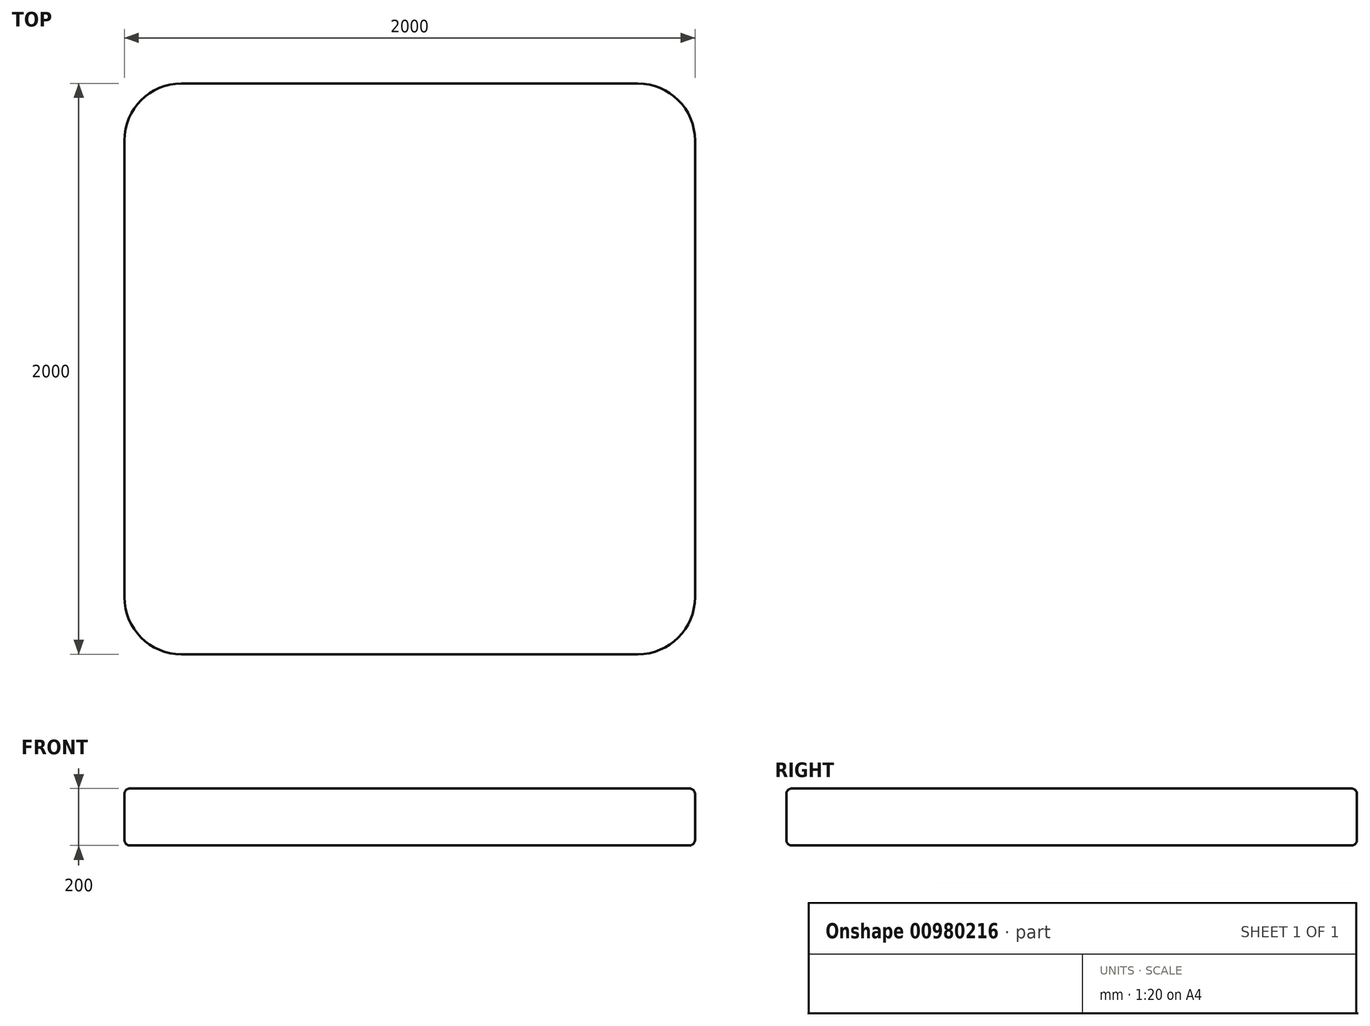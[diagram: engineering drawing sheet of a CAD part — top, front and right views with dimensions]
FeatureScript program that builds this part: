
annotation { "Feature Type Name" : "Feature", "Feature Type Description" : "" }
export const myFeature = defineFeature(function(context is Context, id is Id, definition is map)
    precondition{}
    {
        {
            var Q0;
            Q0=qCreatedBy(makeId("Top.planeOp"),FACE);
            var sketch = newSketch(context, id + "F0", { "sketchPlane" : qUnion([Q0])});
            skLineSegment(sketch, "E0.bottom", {"start": v(1000, -1000) * mm, "end": v(-1000, -1000) * mm});
            skLineSegment(sketch, "E0.top", {"start": v(1000, 1000) * mm, "end": v(-1000, 1000) * mm});
            skLineSegment(sketch, "E0.left", {"start": v(1000, -1000) * mm, "end": v(1000, 1000) * mm});
            skLineSegment(sketch, "E0.right", {"start": v(-1000, -1000) * mm, "end": v(-1000, 1000) * mm});
            skPoint(sketch, "E0.middle", {"position": v(0, 0) * mm});
            skSolve(sketch);
        }
        {
            var Q0;
            Q0=makeQuery(id+"F0.imprint","IMPRINT",FACE,{"disambiguationData":[TD([[makeQuery(id+"F0.imprint","IMPRINT",EDGE,{"derivedFrom":sQuery(id+"F0.wireOp",EDGE,"E0.bottom")}),-1.0]])]});
            extrude(context, id + "F1", {"entities" : qUnion([Q0]), "depth" : 200 * mm, "offsetDistance" : 25 * mm});
        }
        {
            var Q0;
            Q0=makeQuery(id+"F1.opExtrude","CAP_EDGE",EDGE,{"disambiguationData":[OSD([sQuery(id+"F0.wireOp",EDGE,"E0.bottom")])],"isStart":false});
            var Q1;
            Q1=makeQuery(id+"F1.opExtrude","CAP_EDGE",EDGE,{"disambiguationData":[OSD([sQuery(id+"F0.wireOp",EDGE,"E0.right")])],"isStart":false});
            var Q2;
            Q2=makeQuery(id+"F1.opExtrude","CAP_FACE",FACE,{"disambiguationData":[OSD([sQuery(id+"F0.wireOp",EDGE,"E0.bottom"),sQuery(id+"F0.wireOp",EDGE,"E0.top"),sQuery(id+"F0.wireOp",EDGE,"E0.left"),sQuery(id+"F0.wireOp",EDGE,"E0.right")])],"isStart":false});
            var Q3;
            Q3=makeQuery(id+"F1.opExtrude","CAP_EDGE",EDGE,{"disambiguationData":[OSD([sQuery(id+"F0.wireOp",EDGE,"E0.left")])],"isStart":false});
            var Q4;
            Q4=makeQuery(id+"F1.opExtrude","CAP_EDGE",EDGE,{"disambiguationData":[OSD([sQuery(id+"F0.wireOp",EDGE,"E0.left")])],"isStart":true});
            var Q5;
            Q5=makeQuery(id+"F1.opExtrude","CAP_EDGE",EDGE,{"disambiguationData":[OSD([sQuery(id+"F0.wireOp",EDGE,"E0.bottom")])],"isStart":true});
            var Q6;
            Q6=makeQuery(id+"F1.opExtrude","CAP_EDGE",EDGE,{"disambiguationData":[OSD([sQuery(id+"F0.wireOp",EDGE,"E0.right")])],"isStart":true});
            var Q7;
            Q7=makeQuery(id+"F1.opExtrude","CAP_EDGE",EDGE,{"disambiguationData":[OSD([sQuery(id+"F0.wireOp",EDGE,"E0.top")])],"isStart":false});
            var Q8;
            Q8=makeQuery(id+"F1.opExtrude","CAP_EDGE",EDGE,{"disambiguationData":[OSD([sQuery(id+"F0.wireOp",EDGE,"E0.top")])],"isStart":true});
            fillet(context, id + "F2", {"entities" : qUnion([Q0, Q1, Q2, Q3, Q4, Q5, Q6, Q7, Q8]), "radius" : 20 * mm, "tangentPropagation" : true, "allowEdgeOverflow" : false});
        }
        {
            var Q0;
            Q0=makeQuery(id+"F1.opExtrude","SWEPT_EDGE",EDGE,{"disambiguationData":[OSD([sQuery(id+"F0.wireOp",EDGE,"E0.top"),sQuery(id+"F0.wireOp",EDGE,"E0.left")])]});
            var Q1;
            Q1=makeQuery(id+"F1.opExtrude","SWEPT_EDGE",EDGE,{"disambiguationData":[OSD([sQuery(id+"F0.wireOp",EDGE,"E0.bottom"),sQuery(id+"F0.wireOp",EDGE,"E0.left")])]});
            var Q2;
            Q2=makeQuery(id+"F1.opExtrude","SWEPT_EDGE",EDGE,{"disambiguationData":[OSD([sQuery(id+"F0.wireOp",EDGE,"E0.bottom"),sQuery(id+"F0.wireOp",EDGE,"E0.right")])]});
            var Q3;
            Q3=makeQuery(id+"F1.opExtrude","SWEPT_EDGE",EDGE,{"disambiguationData":[OSD([sQuery(id+"F0.wireOp",EDGE,"E0.top"),sQuery(id+"F0.wireOp",EDGE,"E0.right")])]});
            fillet(context, id + "F3", {"entities" : qUnion([Q0, Q1, Q2, Q3]), "radius" : 200 * mm, "tangentPropagation" : true, "allowEdgeOverflow" : false});
        }
    });
